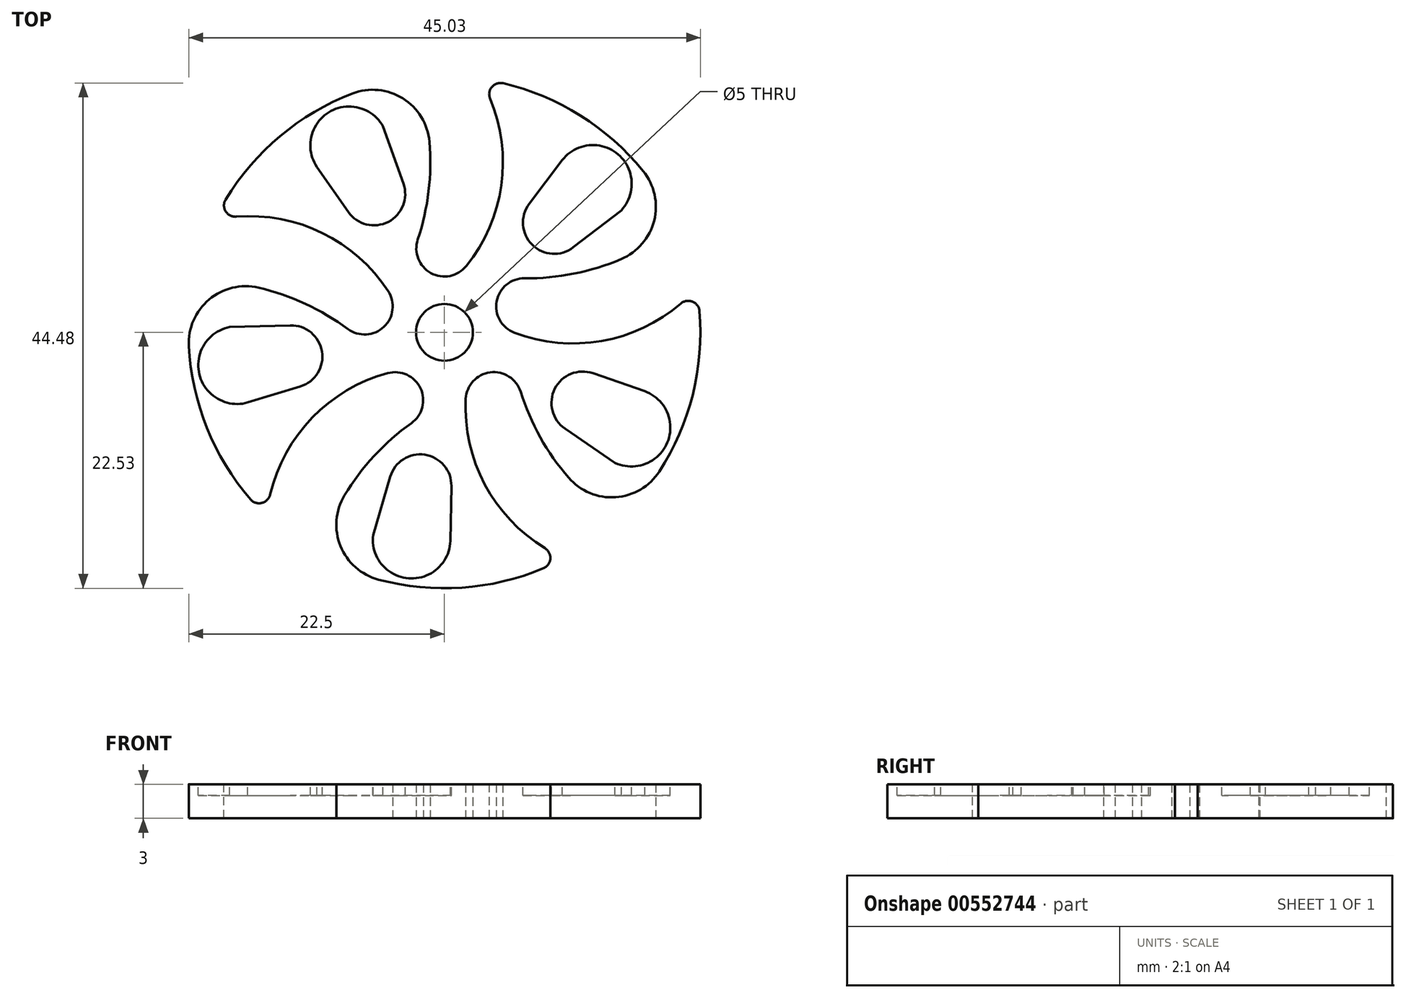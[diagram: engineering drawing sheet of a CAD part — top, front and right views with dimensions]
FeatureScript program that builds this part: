
annotation { "Feature Type Name" : "Feature", "Feature Type Description" : "" }
export const myFeature = defineFeature(function(context is Context, id is Id, definition is map)
    precondition{}
    {
        {
            var Q0;
            Q0=qCreatedBy(makeId("Top.planeOp"),FACE);
            var sketch = newSketch(context, id + "F0", { "sketchPlane" : qUnion([Q0])});
            skLineSegment(sketch, "E0.bottom", {"start": v(0, 0) * mm, "end": v(50, 0) * mm, "construction": true});
            skLineSegment(sketch, "E0.top", {"start": v(0, 50) * mm, "end": v(50, 50) * mm, "construction": true});
            skLineSegment(sketch, "E0.left", {"start": v(0, 0) * mm, "end": v(0, 50) * mm, "construction": true});
            skLineSegment(sketch, "E0.right", {"start": v(50, 0) * mm, "end": v(50, 50) * mm, "construction": true});
            skLineSegment(sketch, "E1", {"start": v(25, 50) * mm, "end": v(25, 0) * mm, "construction": true});
            skLineSegment(sketch, "E2", {"start": v(0, 25) * mm, "end": v(50, 25) * mm, "construction": true});
            skCircle(sketch, "E3", {"center": v(25, 25) * mm, "radius": 2.5 * mm});
            skArc(sketch, "E4", {"start": v(22.65, 33.17) * mm, "mid": v(23.81, 30.22) * mm, "end": v(26.93, 30.84) * mm});
            skArc(sketch, "E5", {"start": v(26.93, 49.08) * mm, "mid": v(23.81, 49.7) * mm, "end": v(22.65, 46.74) * mm});
            skArc(sketch, "E6", {"start": v(26.93, 30.84) * mm, "mid": v(30.14, 39.96) * mm, "end": v(26.93, 49.08) * mm});
            skArc(sketch, "E7", {"start": v(22.65, 33.17) * mm, "mid": v(23.76, 39.96) * mm, "end": v(22.65, 46.74) * mm});
            skArc(sketch, "E8.1.0", {"start": v(20.04, 28.64) * mm, "mid": v(12.36, 34.51) * mm, "end": v(2.7, 34.27) * mm});
            skArc(sketch, "E8.1.1", {"start": v(2.7, 34.27) * mm, "mid": v(1.15, 31.5) * mm, "end": v(3.6, 29.49) * mm});
            skArc(sketch, "E8.1.2", {"start": v(16.5, 25.3) * mm, "mid": v(10.39, 28.44) * mm, "end": v(3.6, 29.49) * mm});
            skArc(sketch, "E8.1.3", {"start": v(16.5, 25.3) * mm, "mid": v(19.67, 25.48) * mm, "end": v(20.04, 28.64) * mm});
            skArc(sketch, "E8.2.0", {"start": v(20, 21.4) * mm, "mid": v(12.05, 15.92) * mm, "end": v(9.29, 6.65) * mm});
            skArc(sketch, "E8.2.1", {"start": v(9.29, 6.65) * mm, "mid": v(11.44, 4.32) * mm, "end": v(14.12, 6.03) * mm});
            skArc(sketch, "E8.2.2", {"start": v(22.1, 17) * mm, "mid": v(17.21, 12.17) * mm, "end": v(14.12, 6.03) * mm});
            skArc(sketch, "E8.2.3", {"start": v(22.1, 17) * mm, "mid": v(22.9, 20.08) * mm, "end": v(20, 21.4) * mm});
            skArc(sketch, "E8.3.0", {"start": v(26.87, 19.14) * mm, "mid": v(29.63, 9.88) * mm, "end": v(37.6, 4.39) * mm});
            skArc(sketch, "E8.3.1", {"start": v(37.6, 4.39) * mm, "mid": v(40.48, 5.72) * mm, "end": v(39.68, 8.79) * mm});
            skArc(sketch, "E8.3.2", {"start": v(31.7, 19.77) * mm, "mid": v(34.8, 13.63) * mm, "end": v(39.68, 8.79) * mm});
            skArc(sketch, "E8.3.3", {"start": v(31.7, 19.77) * mm, "mid": v(29.03, 21.47) * mm, "end": v(26.87, 19.14) * mm});
            skArc(sketch, "E8.4.0", {"start": v(31.15, 24.97) * mm, "mid": v(40.82, 24.73) * mm, "end": v(48.5, 30.6) * mm});
            skArc(sketch, "E8.4.1", {"start": v(48.5, 30.6) * mm, "mid": v(48.12, 33.76) * mm, "end": v(44.95, 33.95) * mm});
            skArc(sketch, "E8.4.2", {"start": v(32.05, 29.76) * mm, "mid": v(38.84, 30.8) * mm, "end": v(44.95, 33.95) * mm});
            skArc(sketch, "E8.4.3", {"start": v(32.05, 29.76) * mm, "mid": v(29.6, 27.74) * mm, "end": v(31.15, 24.97) * mm});
            skCircle(sketch, "E9", {"center": v(25, 25) * mm, "radius": 22.53 * mm});
            skSolve(sketch);
        }
        {
            var Q0;
            Q0=makeQuery(id+"F0.imprint","IMPRINT",FACE,{"disambiguationData":[TD([[makeQuery(id+"F0.imprint","IMPRINT",EDGE,{"derivedFrom":sQuery(id+"F0.wireOp",EDGE,"E3")}),-1.0]])]});
            extrude(context, id + "F1", {"entities" : qUnion([Q0]), "depth" : 3 * mm, "offsetDistance" : 25 * mm});
        }
        {
            var Q0;
            Q0=makeQuery(id+"F1.opExtrude","CAP_FACE",FACE,{"disambiguationData":[OSD([sQuery(id+"F0.wireOp",EDGE,"E3"),sQuery(id+"F0.wireOp",EDGE,"E4"),sQuery(id+"F0.wireOp",EDGE,"E5"),sQuery(id+"F0.wireOp",EDGE,"E6"),sQuery(id+"F0.wireOp",EDGE,"E7"),sQuery(id+"F0.wireOp",EDGE,"E8.1.0"),sQuery(id+"F0.wireOp",EDGE,"E8.1.1"),sQuery(id+"F0.wireOp",EDGE,"E8.1.2"),sQuery(id+"F0.wireOp",EDGE,"E8.1.3"),sQuery(id+"F0.wireOp",EDGE,"E8.2.0"),sQuery(id+"F0.wireOp",EDGE,"E8.2.1"),sQuery(id+"F0.wireOp",EDGE,"E8.2.2"),sQuery(id+"F0.wireOp",EDGE,"E8.2.3"),sQuery(id+"F0.wireOp",EDGE,"E8.3.0"),sQuery(id+"F0.wireOp",EDGE,"E8.3.1"),sQuery(id+"F0.wireOp",EDGE,"E8.3.2"),sQuery(id+"F0.wireOp",EDGE,"E8.3.3"),sQuery(id+"F0.wireOp",EDGE,"E8.4.0"),sQuery(id+"F0.wireOp",EDGE,"E8.4.1"),sQuery(id+"F0.wireOp",EDGE,"E8.4.2"),sQuery(id+"F0.wireOp",EDGE,"E8.4.3"),sQuery(id+"F0.wireOp",EDGE,"E9")])],"isStart":false});
            var sketch = newSketch(context, id + "F2", { "sketchPlane" : qUnion([Q0])});
            skLineSegment(sketch, "E10", {"start": v(25, 25) * mm, "end": v(35.95, 35.95) * mm, "construction": true});
            skLineSegment(sketch, "E11", {"start": v(25, 25) * mm, "end": v(25, 48.97) * mm, "construction": true});
            skArc(sketch, "E12", {"start": v(32.46, 36.31) * mm, "mid": v(32.72, 32.7) * mm, "end": v(36.34, 32.48) * mm});
            skLineSegment(sketch, "E13", {"start": v(35.37, 40.17) * mm, "end": v(32.46, 36.31) * mm});
            skLineSegment(sketch, "E14", {"start": v(40.56, 35.73) * mm, "end": v(36.34, 32.48) * mm});
            skArc(sketch, "E15.trimOffspring", {"start": v(40.56, 35.73) * mm, "mid": v(40.28, 40.66) * mm, "end": v(35.37, 40.17) * mm});
            skLineSegment(sketch, "E16.trimOffspring", {"start": v(36.19, 36.19) * mm, "end": v(41.95, 41.95) * mm, "construction": true});
            skArc(sketch, "E17.1.0", {"start": v(19.6, 43.12) * mm, "mid": v(14.83, 44.37) * mm, "end": v(13.78, 39.55) * mm});
            skLineSegment(sketch, "E17.1.1", {"start": v(13.78, 39.55) * mm, "end": v(16.55, 35.6) * mm});
            skArc(sketch, "E17.1.2", {"start": v(16.55, 35.6) * mm, "mid": v(20.06, 34.73) * mm, "end": v(21.39, 38.1) * mm});
            skLineSegment(sketch, "E17.1.3", {"start": v(19.6, 43.12) * mm, "end": v(21.39, 38.1) * mm});
            skArc(sketch, "E17.2.0", {"start": v(6.1, 25.46) * mm, "mid": v(3.43, 21.31) * mm, "end": v(7.7, 18.82) * mm});
            skLineSegment(sketch, "E17.2.1", {"start": v(7.7, 18.82) * mm, "end": v(12.31, 20.23) * mm});
            skArc(sketch, "E17.2.2", {"start": v(12.31, 20.23) * mm, "mid": v(14.22, 23.3) * mm, "end": v(11.43, 25.61) * mm});
            skLineSegment(sketch, "E17.2.3", {"start": v(6.1, 25.46) * mm, "end": v(11.43, 25.61) * mm});
            skArc(sketch, "E17.3.0", {"start": v(18.72, 7.17) * mm, "mid": v(21.84, 3.35) * mm, "end": v(25.53, 6.64) * mm});
            skLineSegment(sketch, "E17.3.1", {"start": v(25.53, 6.64) * mm, "end": v(25.61, 11.46) * mm});
            skArc(sketch, "E17.3.2", {"start": v(25.61, 11.46) * mm, "mid": v(23.28, 14.23) * mm, "end": v(20.23, 12.29) * mm});
            skLineSegment(sketch, "E17.3.3", {"start": v(18.72, 7.17) * mm, "end": v(20.23, 12.29) * mm});
            skPoint(sketch, "E17.center", {"position": v(25, 25) * mm});
            skArc(sketch, "E18.3.4.0", {"start": v(40.02, 13.52) * mm, "mid": v(44.62, 15.3) * mm, "end": v(42.63, 19.82) * mm});
            skLineSegment(sketch, "E18.4.4.0", {"start": v(42.63, 19.82) * mm, "end": v(38.07, 21.4) * mm});
            skArc(sketch, "E18.7.4.0", {"start": v(38.07, 21.4) * mm, "mid": v(34.71, 20.04) * mm, "end": v(35.62, 16.53) * mm});
            skLineSegment(sketch, "E18.11.4.0", {"start": v(40.02, 13.52) * mm, "end": v(35.62, 16.53) * mm});
            skSolve(sketch);
        }
        {
            var Q0;
            Q0=makeQuery(id+"F2.imprint","IMPRINT",FACE,{"disambiguationData":[TD([[makeQuery(id+"F2.imprint","IMPRINT",EDGE,{"derivedFrom":sQuery(id+"F2.wireOp",EDGE,"E17.1.0")}),1.0]])]});
            var Q1;
            Q1=makeQuery(id+"F2.imprint","IMPRINT",FACE,{"disambiguationData":[TD([[makeQuery(id+"F2.imprint","IMPRINT",EDGE,{"derivedFrom":sQuery(id+"F2.wireOp",EDGE,"E12")}),1.0]])]});
            var Q2;
            Q2=makeQuery(id+"F2.imprint","IMPRINT",FACE,{"disambiguationData":[TD([[makeQuery(id+"F2.imprint","IMPRINT",EDGE,{"derivedFrom":sQuery(id+"F2.wireOp",EDGE,"E18.3.4.0")}),1.0]])]});
            var Q3;
            Q3=makeQuery(id+"F2.imprint","IMPRINT",FACE,{"disambiguationData":[TD([[makeQuery(id+"F2.imprint","IMPRINT",EDGE,{"derivedFrom":sQuery(id+"F2.wireOp",EDGE,"E17.3.0")}),1.0]])]});
            var Q4;
            Q4=makeQuery(id+"F2.imprint","IMPRINT",FACE,{"disambiguationData":[TD([[makeQuery(id+"F2.imprint","IMPRINT",EDGE,{"derivedFrom":sQuery(id+"F2.wireOp",EDGE,"E17.2.0")}),1.0]])]});
            extrude(context, id + "F3", {"entities" : qUnion([Q0, Q1, Q2, Q3, Q4]), "operationType" : NewBodyOperationType.REMOVE, "oppositeDirection" : true, "depth" : 1 * mm, "offsetDistance" : 25 * mm});
        }
        {
            var Q0;
            Q0=makeQuery(id+"F1.opExtrude","SWEPT_EDGE",EDGE,{"disambiguationData":[OSD([sQuery(id+"F0.wireOp",EDGE,"E8.1.0"),sQuery(id+"F0.wireOp",EDGE,"E9")])]});
            var Q1;
            Q1=makeQuery(id+"F1.opExtrude","SWEPT_EDGE",EDGE,{"disambiguationData":[OSD([sQuery(id+"F0.wireOp",EDGE,"E8.2.0"),sQuery(id+"F0.wireOp",EDGE,"E9")])]});
            var Q2;
            Q2=makeQuery(id+"F1.opExtrude","SWEPT_EDGE",EDGE,{"disambiguationData":[OSD([sQuery(id+"F0.wireOp",EDGE,"E8.3.0"),sQuery(id+"F0.wireOp",EDGE,"E9")])]});
            var Q3;
            Q3=makeQuery(id+"F1.opExtrude","SWEPT_EDGE",EDGE,{"disambiguationData":[OSD([sQuery(id+"F0.wireOp",EDGE,"E8.4.0"),sQuery(id+"F0.wireOp",EDGE,"E9")])]});
            var Q4;
            Q4=makeQuery(id+"F1.opExtrude","SWEPT_EDGE",EDGE,{"disambiguationData":[OSD([sQuery(id+"F0.wireOp",EDGE,"E6"),sQuery(id+"F0.wireOp",EDGE,"E9")])]});
            fillet(context, id + "F4", {"entities" : qUnion([Q0, Q1, Q2, Q3, Q4]), "radius" : 1 * mm, "tangentPropagation" : true, "allowEdgeOverflow" : false});
        }
        {
            var Q0;
            Q0=makeQuery(id+"F1.opExtrude","SWEPT_EDGE",EDGE,{"disambiguationData":[OSD([sQuery(id+"F0.wireOp",EDGE,"E8.2.1"),sQuery(id+"F0.wireOp",EDGE,"E9")])]});
            var Q1;
            Q1=makeQuery(id+"F1.opExtrude","SWEPT_EDGE",EDGE,{"disambiguationData":[OSD([sQuery(id+"F0.wireOp",EDGE,"E8.1.1"),sQuery(id+"F0.wireOp",EDGE,"E9")])]});
            var Q2;
            Q2=makeQuery(id+"F1.opExtrude","SWEPT_EDGE",EDGE,{"disambiguationData":[OSD([sQuery(id+"F0.wireOp",EDGE,"E5"),sQuery(id+"F0.wireOp",EDGE,"E9")])]});
            var Q3;
            Q3=makeQuery(id+"F1.opExtrude","SWEPT_EDGE",EDGE,{"disambiguationData":[OSD([sQuery(id+"F0.wireOp",EDGE,"E8.4.1"),sQuery(id+"F0.wireOp",EDGE,"E9")])]});
            var Q4;
            Q4=makeQuery(id+"F1.opExtrude","SWEPT_EDGE",EDGE,{"disambiguationData":[OSD([sQuery(id+"F0.wireOp",EDGE,"E8.3.1"),sQuery(id+"F0.wireOp",EDGE,"E9")])]});
            fillet(context, id + "F5", {"entities" : qUnion([Q0, Q1, Q2, Q3, Q4]), "radius" : 5 * mm, "tangentPropagation" : true, "allowEdgeOverflow" : false});
        }
    });
